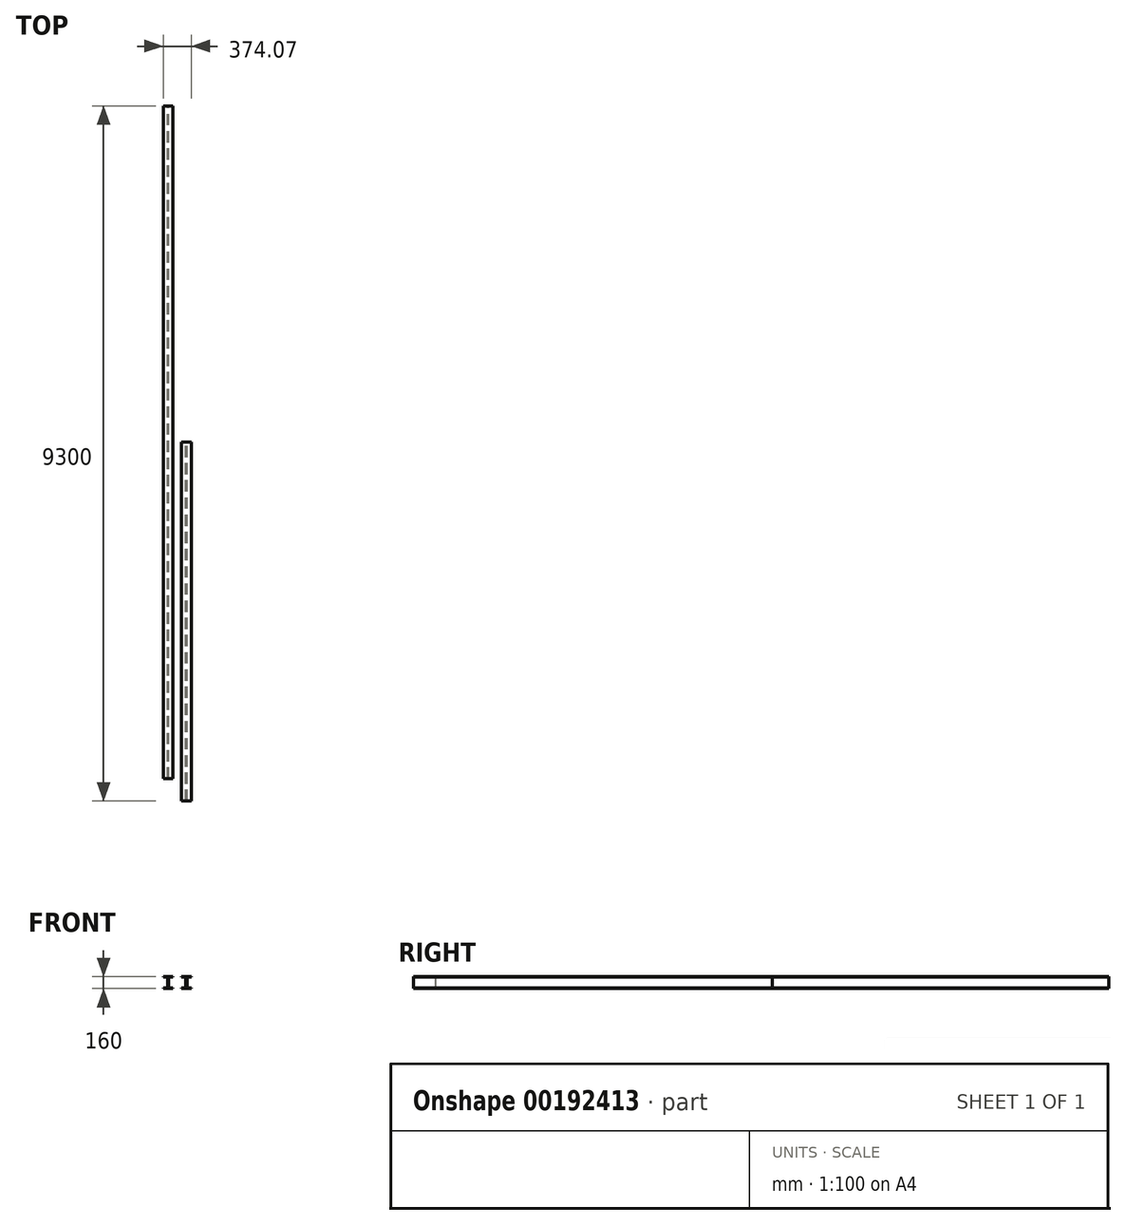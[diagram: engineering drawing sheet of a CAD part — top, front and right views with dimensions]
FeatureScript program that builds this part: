
annotation { "Feature Type Name" : "Feature", "Feature Type Description" : "" }
export const myFeature = defineFeature(function(context is Context, id is Id, definition is map)
    precondition{}
    {
        {
            var Q0;
            Q0=qCreatedBy(makeId("Front.planeOp"),FACE);
            var sketch = newSketch(context, id + "F0", { "sketchPlane" : qUnion([Q0])});
            skLineSegment(sketch, "E0", {"start": v(-8, -64) * mm, "end": v(-8, 80) * mm});
            skLineSegment(sketch, "E1", {"start": v(-8, 80) * mm, "end": v(65, 80) * mm});
            skLineSegment(sketch, "E2", {"start": v(65, 80) * mm, "end": v(65, 88) * mm});
            skLineSegment(sketch, "E3", {"start": v(-8, -64) * mm, "end": v(65, -64) * mm});
            skLineSegment(sketch, "E4", {"start": v(65, -64) * mm, "end": v(65, -72) * mm});
            skLineSegment(sketch, "E5.MirrorCS", {"start": v(8, -64) * mm, "end": v(8, 80) * mm});
            skLineSegment(sketch, "E6.MirrorCS", {"start": v(8, 80) * mm, "end": v(-65, 80) * mm});
            skLineSegment(sketch, "E7.MirrorCS", {"start": v(-65, 80) * mm, "end": v(-65, 88) * mm});
            skLineSegment(sketch, "E8.MirrorCS", {"start": v(8, -64) * mm, "end": v(-65, -64) * mm});
            skLineSegment(sketch, "E9.MirrorCS", {"start": v(-65, -64) * mm, "end": v(-65, -72) * mm});
            skLineSegment(sketch, "E10", {"start": v(-65, -72) * mm, "end": v(65, -72) * mm});
            skLineSegment(sketch, "E11", {"start": v(-65, 88) * mm, "end": v(65, 88) * mm});
            skLineSegment(sketch, "E12.bottom", {"start": v(236.07, 80) * mm, "end": v(252.07, 80) * mm});
            skLineSegment(sketch, "E12.top", {"start": v(236.07, -64) * mm, "end": v(252.07, -64) * mm});
            skLineSegment(sketch, "E12.left", {"start": v(236.07, 80) * mm, "end": v(236.07, -64) * mm});
            skLineSegment(sketch, "E12.right", {"start": v(252.07, 80) * mm, "end": v(252.07, -64) * mm});
            skLineSegment(sketch, "E13.bottom", {"start": v(179.07, 80) * mm, "end": v(309.07, 80) * mm});
            skLineSegment(sketch, "E13.top", {"start": v(179.07, 88) * mm, "end": v(309.07, 88) * mm});
            skLineSegment(sketch, "E13.left", {"start": v(179.07, 80) * mm, "end": v(179.07, 88) * mm});
            skLineSegment(sketch, "E13.right", {"start": v(309.07, 80) * mm, "end": v(309.07, 88) * mm});
            skLineSegment(sketch, "E14.bottom", {"start": v(179.07, -64) * mm, "end": v(309.07, -64) * mm});
            skLineSegment(sketch, "E14.top", {"start": v(179.07, -72) * mm, "end": v(309.07, -72) * mm});
            skLineSegment(sketch, "E14.left", {"start": v(179.07, -64) * mm, "end": v(179.07, -72) * mm});
            skLineSegment(sketch, "E14.right", {"start": v(309.07, -64) * mm, "end": v(309.07, -72) * mm});
            skPoint(sketch, "E15", {"position": v(244.07, 80) * mm});
            skPoint(sketch, "E16", {"position": v(244.07, -64) * mm});
            skSolve(sketch);
        }
        {
            var Q0;
            {var subQ3=sQuery(id+"F0.wireOp",EDGE,"E1");Q0=makeQuery(id+"F0.imprint","IMPRINT",FACE,{"disambiguationData":[TD([[makeQuery(id+"F0.imprint","IMPRINT",EDGE,{"derivedFrom":subQ3}),1.0]])]});}
            var Q1;
            {var subQ0=sQuery(id+"F0.wireOp",EDGE,"E0");Q1=makeQuery(id+"F0.imprint","IMPRINT",FACE,{"disambiguationData":[TD([[makeQuery(id+"F0.imprint","IMPRINT",EDGE,{"derivedFrom":subQ0}),-1.0]])]});}
            var Q2;
            {var subQ3=sQuery(id+"F0.wireOp",EDGE,"E3");Q2=makeQuery(id+"F0.imprint","IMPRINT",FACE,{"disambiguationData":[TD([[makeQuery(id+"F0.imprint","IMPRINT",EDGE,{"derivedFrom":subQ3}),-1.0]])]});}
            extrude(context, id + "F1", {"entities" : qUnion([Q0, Q1, Q2]), "depth" : 9000 * mm, "symmetric" : true});
        }
        {
            var Q0;
            Q0=makeQuery(id+"F0.imprint","IMPRINT",FACE,{"disambiguationData":[TD([[makeQuery(id+"F0.imprint","IMPRINT",EDGE,{"derivedFrom":sQuery(id+"F0.wireOp",EDGE,"E13.top")}),-1.0]])]});
            var Q1;
            {var subQ0=sQuery(id+"F0.wireOp",EDGE,"E12.left");Q1=makeQuery(id+"F0.imprint","IMPRINT",FACE,{"disambiguationData":[TD([[makeQuery(id+"F0.imprint","IMPRINT",EDGE,{"derivedFrom":subQ0}),1.0]])]});}
            var Q2;
            Q2=makeQuery(id+"F0.imprint","IMPRINT",FACE,{"disambiguationData":[TD([[makeQuery(id+"F0.imprint","IMPRINT",EDGE,{"derivedFrom":sQuery(id+"F0.wireOp",EDGE,"E14.top")}),1.0]])]});
            extrude(context, id + "F2", {"entities" : qUnion([Q0, Q1, Q2]), "depth" : 4800 * mm});
        }
    });
